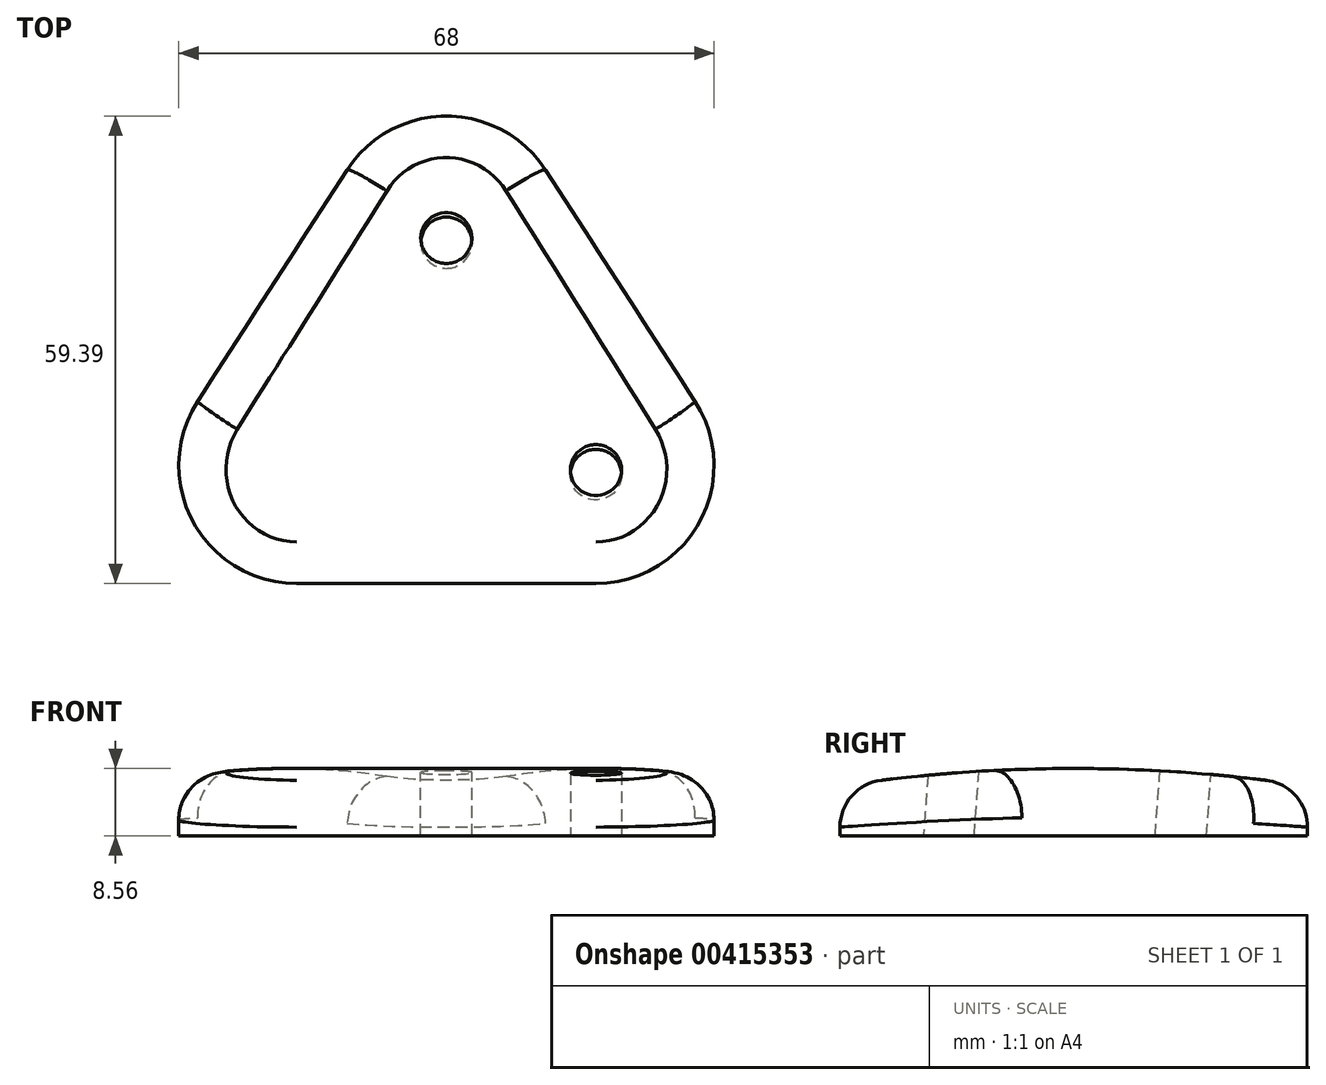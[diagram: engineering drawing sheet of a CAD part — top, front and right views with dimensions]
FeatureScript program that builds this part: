
annotation { "Feature Type Name" : "Feature", "Feature Type Description" : "" }
export const myFeature = defineFeature(function(context is Context, id is Id, definition is map)
    precondition{}
    {
        {
            var Q0;
            Q0=qCreatedBy(makeId("Top.planeOp"),FACE);
            var sketch = newSketch(context, id + "F0", { "sketchPlane" : qUnion([Q0])});
            skArc(sketch, "E0", {"start": v(-31.6, 8.14) * mm, "mid": v(-32.17, -7.17) * mm, "end": v(-19, -15) * mm});
            skArc(sketch, "E1", {"start": v(19, -15) * mm, "mid": v(32.17, -7.17) * mm, "end": v(31.6, 8.14) * mm});
            skArc(sketch, "E2", {"start": v(12.6, 37.54) * mm, "mid": v(0, 44.4) * mm, "end": v(-12.6, 37.54) * mm});
            skLineSegment(sketch, "E3", {"start": v(-31.6, 8.14) * mm, "end": v(-12.6, 37.54) * mm});
            skLineSegment(sketch, "E4", {"start": v(12.6, 37.54) * mm, "end": v(31.6, 8.14) * mm});
            skLineSegment(sketch, "E5", {"start": v(19, -15) * mm, "end": v(-19, -15) * mm});
            skSolve(sketch);
        }
        {
            var Q0;
            Q0=makeQuery(id+"F0.imprint","IMPRINT",FACE,{"disambiguationData":[TD([[makeQuery(id+"F0.imprint","IMPRINT",EDGE,{"derivedFrom":sQuery(id+"F0.wireOp",EDGE,"btSFY6ni-hCM5-hNcQ-g6QM-1PdfdnVNjnFe")}),-1.0]])]});
            var Q1;
            Q1=makeQuery(id+"F0.imprint","IMPRINT",FACE,{"disambiguationData":[TD([[makeQuery(id+"F0.imprint","IMPRINT",EDGE,{"derivedFrom":sQuery(id+"F0.wireOp",EDGE,"E0")}),1.0]])]});
            extrude(context, id + "F1", {"entities" : qUnion([Q0, Q1]), "depth" : 10 * mm});
        }
        {
            var Q0;
            Q0=qCreatedBy(makeId("Right.planeOp"),FACE);
            var sketch = newSketch(context, id + "F2", { "sketchPlane" : qUnion([Q0])});
            skLineSegment(sketch, "E6.bottom", {"start": v(-20.3, -3.08) * mm, "end": v(49.7, -3.08) * mm});
            skLineSegment(sketch, "E6.top", {"start": v(-20.3, 14.04) * mm, "end": v(49.7, 14.04) * mm});
            skLineSegment(sketch, "E6.left", {"start": v(-20.3, -3.08) * mm, "end": v(-20.3, 14.04) * mm});
            skLineSegment(sketch, "E6.right", {"start": v(49.7, -3.08) * mm, "end": v(49.7, 14.04) * mm});
            skArc(sketch, "E7", {"start": v(49.7, 5.48) * mm, "mid": v(14.7, 8.56) * mm, "end": v(-20.3, 5.48) * mm});
            skLineSegment(sketch, "E8", {"start": v(0, 8.02) * mm, "end": v(0.44, 2.04) * mm});
            skLineSegment(sketch, "E9", {"start": v(29.4, 8.02) * mm, "end": v(29.06, 3.46) * mm});
            skSolve(sketch);
        }
        {
            var Q0;
            {var subQ0=sQuery(id+"F2.wireOp",EDGE,"E6.top");Q0=makeQuery(id+"F2.imprint","IMPRINT",FACE,{"disambiguationData":[TD([[makeQuery(id+"F2.imprint","IMPRINT",EDGE,{"derivedFrom":subQ0}),-1.0]])]});}
            extrude(context, id + "F3", {"entities" : qUnion([Q0]), "operationType" : NewBodyOperationType.REMOVE, "endBound" : BoundingType.SYMMETRIC, "oppositeDirection" : true, "depth" : 70 * mm});
        }
        {
            var Q0;
            Q0=sQuery(id+"F2.wireOp",EDGE,"E8");
            var Q1;
            Q1=sQuery(id+"F2.wireOp",VERTEX,"E8.start");
            cPlane(context, id + "F4", {"entities" : qUnion([Q0, Q1]), "cplaneType" : CPlaneType.LINE_POINT, "offset" : 25 * mm, "width" : 150 * mm, "height" : 150 * mm});
        }
        {
            var Q0;
            Q0=qCreatedBy(id+"F4.planeOp",FACE);
            var sketch = newSketch(context, id + "F5", { "sketchPlane" : qUnion([Q0])});
            skCircle(sketch, "E10", {"center": v(19, 0) * mm, "radius": 3.25 * mm});
            skCircle(sketch, "E11.MirrorC", {"center": v(-19, 0) * mm, "radius": 3.25 * mm});
            skSolve(sketch);
        }
        {
            var Q0;
            Q0=sQuery(id+"F2.wireOp",VERTEX,"E9.start");
            var Q1;
            Q1=sQuery(id+"F2.wireOp",EDGE,"E9");
            cPlane(context, id + "F6", {"entities" : qUnion([Q0, Q1]), "cplaneType" : CPlaneType.LINE_POINT, "offset" : 25 * mm, "width" : 150 * mm, "height" : 150 * mm});
        }
        {
            var Q0;
            Q0=qCreatedBy(id+"F6.planeOp",FACE);
            var sketch = newSketch(context, id + "F7", { "sketchPlane" : qUnion([Q0])});
            skCircle(sketch, "E12", {"center": v(0, -28.22) * mm, "radius": 3.25 * mm});
            skSolve(sketch);
        }
        {
            var Q0;
            Q0=makeQuery(id+"F5.imprint","IMPRINT",FACE,{"disambiguationData":[TD([[makeQuery(id+"F5.imprint","IMPRINT",EDGE,{"derivedFrom":sQuery(id+"F5.wireOp",EDGE,"E11.MirrorC")}),-1.0]])]});
            var Q1;
            Q1=makeQuery(id+"F7.imprint","IMPRINT",FACE,{"disambiguationData":[TD([[makeQuery(id+"F7.imprint","IMPRINT",EDGE,{"derivedFrom":sQuery(id+"F7.wireOp",EDGE,"E12")}),1.0]])]});
            var Q2;
            Q2=makeQuery(id+"F5.imprint","IMPRINT",FACE,{"disambiguationData":[TD([[makeQuery(id+"F5.imprint","IMPRINT",EDGE,{"derivedFrom":sQuery(id+"F5.wireOp",EDGE,"E10")}),1.0]])]});
            extrude(context, id + "F8", {"entities" : qUnion([Q0, Q1, Q2]), "operationType" : NewBodyOperationType.REMOVE, "endBound" : BoundingType.SYMMETRIC, "depth" : 25 * mm});
        }
        {
            var Q0;
            Q0=makeQuery(id+"F3.boolean.opBoolean","INTERSECT",EDGE,{"derivedFrom":[makeQuery(id+"F1.opExtrude","SWEPT_FACE",FACE,{"disambiguationData":[OSD([sQuery(id+"F0.wireOp",EDGE,"E1")])]}),makeQuery(id+"F3.opExtrude","SWEPT_FACE",FACE,{"disambiguationData":[OSD([sQuery(id+"F2.wireOp",EDGE,"E7")])]})]});
            var Q1;
            Q1=makeQuery(id+"F3.boolean.opBoolean","INTERSECT",EDGE,{"derivedFrom":[makeQuery(id+"F1.opExtrude","SWEPT_FACE",FACE,{"disambiguationData":[OSD([sQuery(id+"F0.wireOp",EDGE,"E4")])]}),makeQuery(id+"F3.opExtrude","SWEPT_FACE",FACE,{"disambiguationData":[OSD([sQuery(id+"F2.wireOp",EDGE,"E7")])]})]});
            fillet(context, id + "F9", {"entities" : qUnion([Q0, Q1]), "radius" : 6 * mm, "tangentPropagation" : true, "allowEdgeOverflow" : false});
        }
    });
